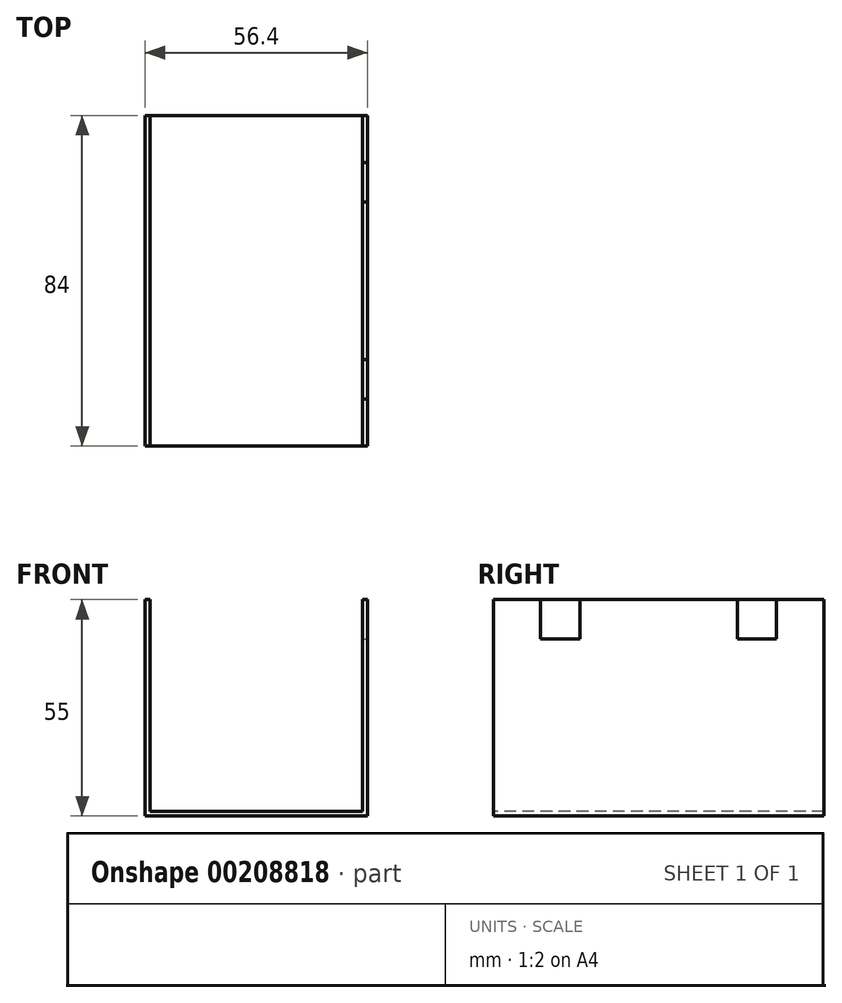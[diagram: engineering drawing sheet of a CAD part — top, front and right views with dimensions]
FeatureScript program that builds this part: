
annotation { "Feature Type Name" : "Feature", "Feature Type Description" : "" }
export const myFeature = defineFeature(function(context is Context, id is Id, definition is map)
    precondition{}
    {
        {
            var Q0;
            Q0=qCreatedBy(makeId("Top.planeOp"),FACE);
            var sketch = newSketch(context, id + "F0", { "sketchPlane" : qUnion([Q0])});
            skLineSegment(sketch, "E0.bottom", {"start": v(-27, 42) * mm, "end": v(27, 42) * mm});
            skLineSegment(sketch, "E0.top", {"start": v(-27, -42) * mm, "end": v(27, -42) * mm});
            skLineSegment(sketch, "E0.left", {"start": v(-27, 42) * mm, "end": v(-27, -42) * mm});
            skLineSegment(sketch, "E0.right", {"start": v(27, 42) * mm, "end": v(27, -42) * mm});
            skPoint(sketch, "E0.middle", {"position": v(0, 0) * mm});
            skLineSegment(sketch, "E1.bottom", {"start": v(28.2, 42) * mm, "end": v(-28.2, 42) * mm});
            skLineSegment(sketch, "E1.top", {"start": v(28.2, -42) * mm, "end": v(-28.2, -42) * mm});
            skLineSegment(sketch, "E1.left", {"start": v(28.2, 42) * mm, "end": v(28.2, -42) * mm});
            skLineSegment(sketch, "E1.right", {"start": v(-28.2, 42) * mm, "end": v(-28.2, -42) * mm});
            skSolve(sketch);
        }
        {
            var Q0;
            Q0=makeQuery(id+"F0.imprint","IMPRINT",FACE,{"disambiguationData":[TD([[makeQuery(id+"F0.imprint","IMPRINT",EDGE,{"derivedFrom":sQuery(id+"F0.wireOp",EDGE,"E0.bottom")}),-1.0]])]});
            extrude(context, id + "F1", {"entities" : qUnion([Q0]), "depth" : 1.2 * mm});
        }
        {
            var Q0;
            {var subQ0=sQuery(id+"F0.wireOp",EDGE,"E0.left");Q0=makeQuery(id+"F0.imprint","IMPRINT",FACE,{"disambiguationData":[TD([[makeQuery(id+"F0.imprint","IMPRINT",EDGE,{"derivedFrom":subQ0}),-1.0]])]});}
            var Q1;
            {var subQ0=sQuery(id+"F0.wireOp",EDGE,"E0.right");Q1=makeQuery(id+"F0.imprint","IMPRINT",FACE,{"disambiguationData":[TD([[makeQuery(id+"F0.imprint","IMPRINT",EDGE,{"derivedFrom":subQ0}),1.0]])]});}
            extrude(context, id + "F2", {"entities" : qUnion([Q0, Q1]), "operationType" : NewBodyOperationType.ADD, "depth" : 55 * mm});
        }
        {
            var Q0;
            Q0=makeQuery(id+"F2.opExtrude","SWEPT_FACE",FACE,{"disambiguationData":[OSD([sQuery(id+"F0.wireOp",EDGE,"E1.left")])]});
            var sketch = newSketch(context, id + "F3", { "sketchPlane" : qUnion([Q0])});
            skLineSegment(sketch, "E2.bottom", {"start": v(-30, 55) * mm, "end": v(-20, 55) * mm});
            skLineSegment(sketch, "E2.top", {"start": v(-30, 45) * mm, "end": v(-20, 45) * mm});
            skLineSegment(sketch, "E2.left", {"start": v(-30, 55) * mm, "end": v(-30, 45) * mm});
            skLineSegment(sketch, "E2.right", {"start": v(-20, 55) * mm, "end": v(-20, 45) * mm});
            skLineSegment(sketch, "E3.MirrorCS", {"start": v(20, 55) * mm, "end": v(20, 45) * mm});
            skLineSegment(sketch, "E4.MirrorCS", {"start": v(30, 45) * mm, "end": v(20, 45) * mm});
            skLineSegment(sketch, "E5.MirrorCS", {"start": v(30, 55) * mm, "end": v(30, 45) * mm});
            skSolve(sketch);
        }
        {
            var Q0;
            Q0=makeQuery(id+"F3.imprint","IMPRINT",FACE,{"disambiguationData":[TD([[makeQuery(id+"F3.imprint","IMPRINT",EDGE,{"derivedFrom":sQuery(id+"F3.wireOp",EDGE,"E2.bottom")}),1.0]])]});
            var Q1;
            {var subQ0=sQuery(id+"F3.wireOp",EDGE,"E3.MirrorCS");Q1=makeQuery(id+"F3.imprint","IMPRINT",FACE,{"disambiguationData":[TD([[makeQuery(id+"F3.imprint","IMPRINT",EDGE,{"derivedFrom":subQ0}),1.0]])]});}
            extrude(context, id + "F4", {"entities" : qUnion([Q0, Q1]), "operationType" : NewBodyOperationType.REMOVE, "oppositeDirection" : true, "depth" : 25 * mm});
        }
    });
